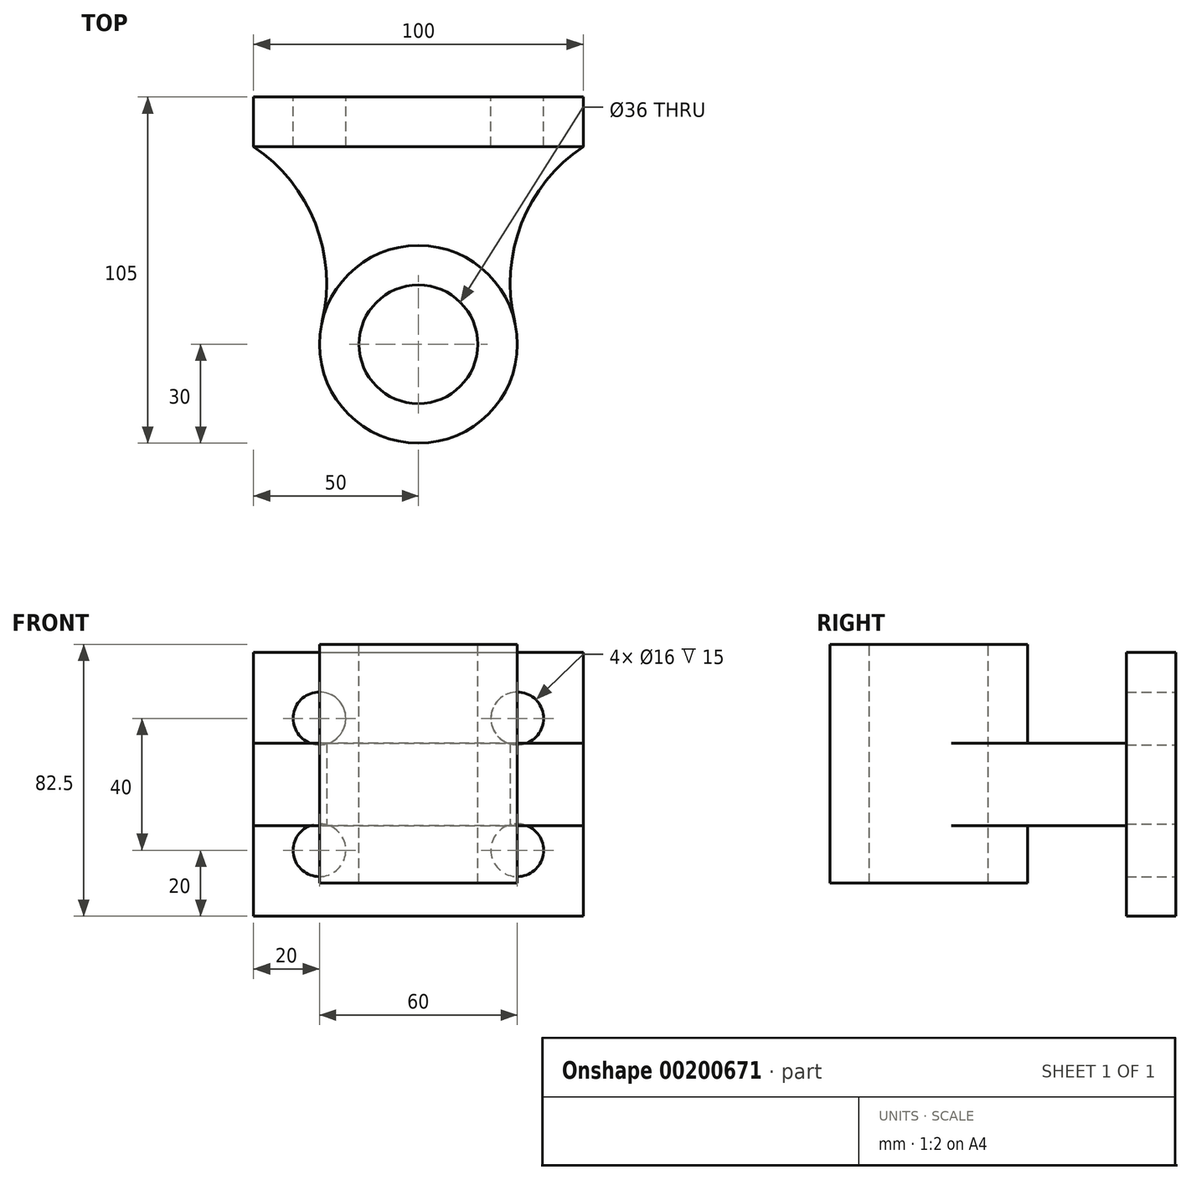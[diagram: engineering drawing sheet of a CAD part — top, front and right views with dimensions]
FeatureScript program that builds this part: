
annotation { "Feature Type Name" : "Feature", "Feature Type Description" : "" }
export const myFeature = defineFeature(function(context is Context, id is Id, definition is map)
    precondition{}
    {
        {
            var Q0;
            Q0=qCreatedBy(makeId("Front.planeOp"),FACE);
            var sketch = newSketch(context, id + "F0", { "sketchPlane" : qUnion([Q0])});
            skLineSegment(sketch, "E0.bottom", {"start": v(-50, 40) * mm, "end": v(50, 40) * mm});
            skLineSegment(sketch, "E0.top", {"start": v(-50, -40) * mm, "end": v(50, -40) * mm});
            skLineSegment(sketch, "E0.left", {"start": v(-50, 40) * mm, "end": v(-50, -40) * mm});
            skLineSegment(sketch, "E0.right", {"start": v(50, 40) * mm, "end": v(50, -40) * mm});
            skCircle(sketch, "E1", {"center": v(-30, 20) * mm, "radius": 8 * mm});
            skCircle(sketch, "E2", {"center": v(30, 20) * mm, "radius": 8 * mm});
            skCircle(sketch, "E3", {"center": v(30, -20) * mm, "radius": 8 * mm});
            skCircle(sketch, "E4", {"center": v(-30, -20) * mm, "radius": 8 * mm});
            skSolve(sketch);
        }
        {
            var Q0;
            Q0 = qSketchRegion(id + "F0", true);
            extrude(context, id + "F1", {"entities" : qUnion([Q0]), "depth" : 15 * mm});
        }
        {
            var Q0;
            Q0=makeQuery(id+"F1.opExtrude","SWEPT_FACE",FACE,{"disambiguationData":[OSD([sQuery(id+"F0.wireOp",EDGE,"E0.top")])]});
            cPlane(context, id + "F2", {"entities" : qUnion([Q0]), "cplaneType" : CPlaneType.OFFSET, "offset" : 40 * mm, "oppositeDirection" : true, "width" : 150 * mm, "height" : 150 * mm});
        }
        {
            var Q0;
            Q0=qCreatedBy(id+"F2.planeOp",FACE);
            var sketch = newSketch(context, id + "F3", { "sketchPlane" : qUnion([Q0])});
            skCircle(sketch, "E5", {"center": v(0, 75) * mm, "radius": 30 * mm});
            skCircle(sketch, "E6", {"center": v(0, 75) * mm, "radius": 18 * mm});
            skSolve(sketch);
        }
        {
            var Q0;
            Q0=makeQuery(id+"F3.imprint","IMPRINT",FACE,{"disambiguationData":[TD([[makeQuery(id+"F3.imprint","IMPRINT",EDGE,{"derivedFrom":sQuery(id+"F3.wireOp",EDGE,"E5")}),1.0]])]});
            extrude(context, id + "F4", {"entities" : qUnion([Q0]), "endBound" : BoundingType.SYMMETRIC, "depth" : 60 * mm});
        }
        {
            var Q0;
            Q0=qCreatedBy(makeId("Top.planeOp"),FACE);
            var sketch = newSketch(context, id + "F5", { "sketchPlane" : qUnion([Q0])});
            skArc(sketch, "E7", {"start": v(50, -15) * mm, "mid": v(31.29, -38.28) * mm, "end": v(29.19, -68.07) * mm});
            skArc(sketch, "E8", {"start": v(-29.19, -68.07) * mm, "mid": v(-31.29, -38.28) * mm, "end": v(-50, -15) * mm});
            skCircle(sketch, "E9.0", {"center": v(0, -75) * mm, "radius": 30 * mm});
            skLineSegment(sketch, "E10.0", {"start": v(-50, -15) * mm, "end": v(50, -15) * mm});
            skSolve(sketch);
        }
        {
            var Q0;
            {var subQ0=sQuery(id+"F5.wireOp",EDGE,"E7");Q0=makeQuery(id+"F5.imprint","IMPRINT",FACE,{"disambiguationData":[TD([[makeQuery(id+"F5.imprint","IMPRINT",EDGE,{"derivedFrom":subQ0}),-1.0]])]});}
            extrude(context, id + "F6", {"entities" : qUnion([Q0]), "endBound" : BoundingType.SYMMETRIC, "depth" : 10 * mm});
        }
        {
            var Q0;
            {var subQ0=sQuery(id+"F5.wireOp",EDGE,"E7");Q0=makeQuery(id+"F5.imprint","IMPRINT",FACE,{"disambiguationData":[TD([[makeQuery(id+"F5.imprint","IMPRINT",EDGE,{"derivedFrom":subQ0}),-1.0]])]});}
            var Q1;
            Q1=makeQuery(id+"F4.opExtrude","CAP_FACE",FACE,{"disambiguationData":[OSD([sQuery(id+"F3.wireOp",EDGE,"E5"),sQuery(id+"F3.wireOp",EDGE,"E6")])],"isStart":true});
            extrude(context, id + "F7", {"entities" : qUnion([Q0, Q1]), "operationType" : NewBodyOperationType.ADD, "endBound" : BoundingType.SYMMETRIC, "depth" : 25 * mm});
        }
    });
